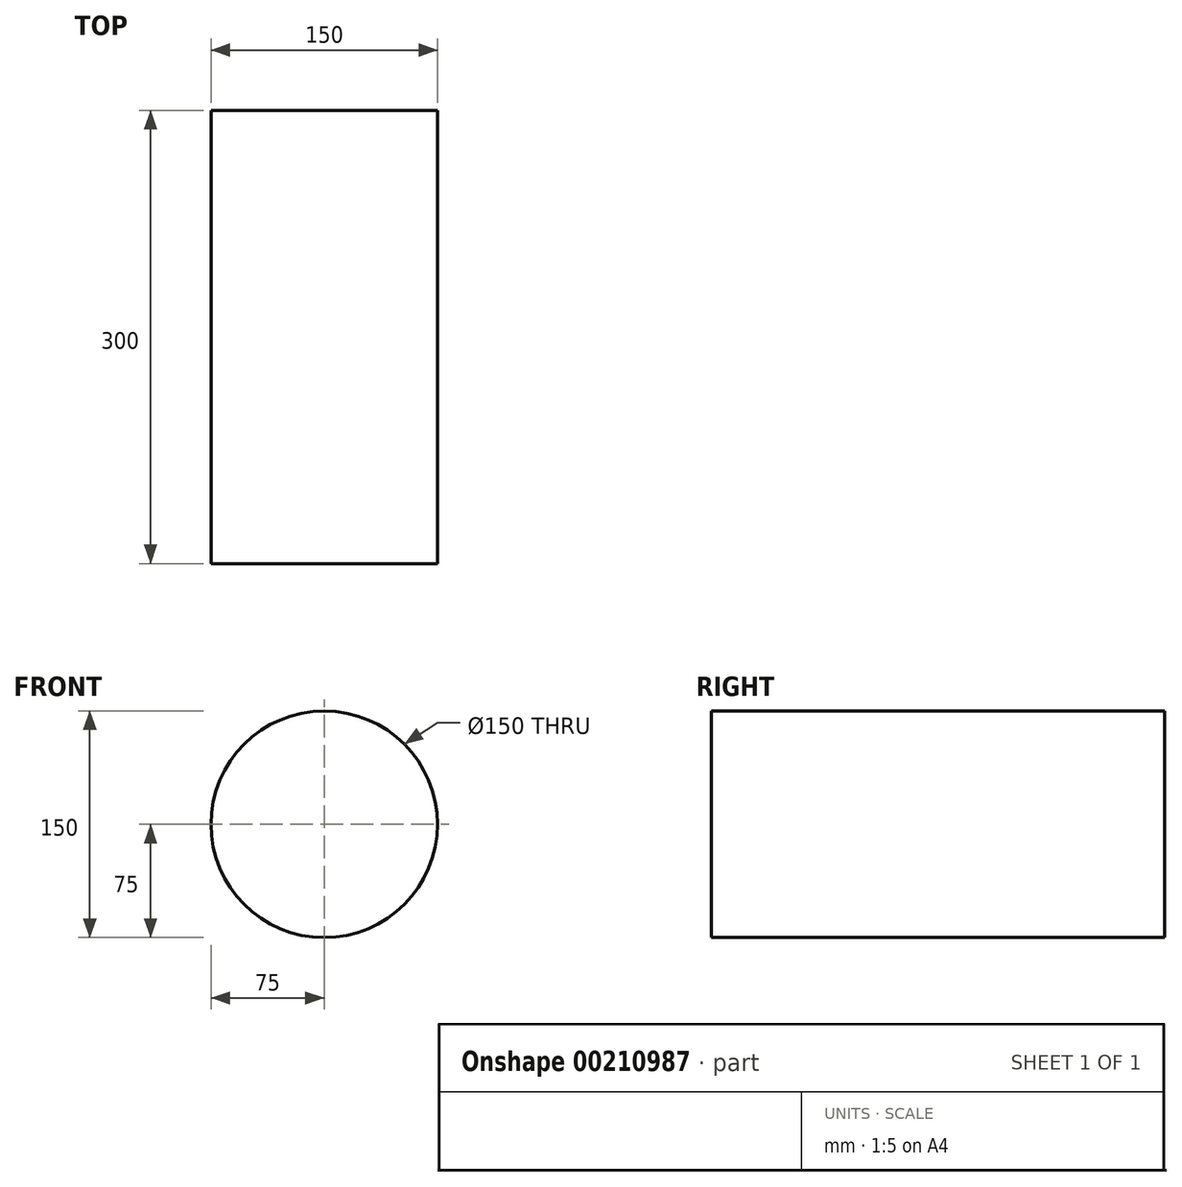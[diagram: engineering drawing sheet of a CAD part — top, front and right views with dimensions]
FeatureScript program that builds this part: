
annotation { "Feature Type Name" : "Feature", "Feature Type Description" : "" }
export const myFeature = defineFeature(function(context is Context, id is Id, definition is map)
    precondition{}
    {
        {
            var Q0;
            Q0=qCreatedBy(makeId("Front.planeOp"),FACE);
            var sketch = newSketch(context, id + "F0", { "sketchPlane" : qUnion([Q0])});
            skCircle(sketch, "E0", {"center": v(0, 0) * mm, "radius": 75 * mm});
            skCircle(sketch, "E1", {"center": v(0, 0) * mm, "radius": 74 * mm});
            skSolve(sketch);
        }
        {
            var Q0;
            Q0=sQuery(id+"F0.wireOp",EDGE,"E0");
            extrude(context, id + "F1", {"bodyType" : ToolBodyType.SURFACE, "surfaceEntities" : qUnion([Q0]), "oppositeDirection" : true, "depth" : 300 * mm, "offsetDistance" : 25 * mm});
        }
    });
